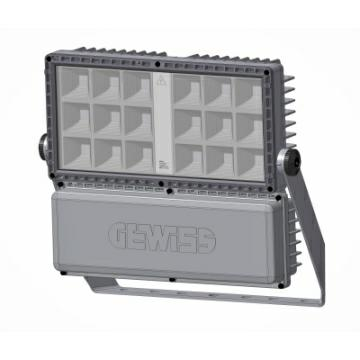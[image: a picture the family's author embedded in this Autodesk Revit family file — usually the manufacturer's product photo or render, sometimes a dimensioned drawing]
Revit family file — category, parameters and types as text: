
# Revit family: Lighting-Floodlights-GEWISS-SMART[PRO]2.0-LED-MEDIUM-POWER_1MODULE_DALI.CLI
name_source: partatom
category: Apparecchi per illuminazione
units: mm (PartAtom-declared; Revit-internal decimal feet)

## family parameters
Condiviso = No
Host = Superficie
Punto di calcolo locali = Sì
Quota connettore circolare = Usa diametro
Sorgente d'illuminazione = No
Taglio con vuoti quando caricato = No
Tipo di parte = Normale

## types (1)
- Lighting-Floodlights-GEWISS-SMART[PRO]2.0-LED-MEDIUM-POWER_1MODULE_DALI.CLI
    Applicazione = Indoor / Outdoor
    Body = Die-cast aluminium -
    Catalogue = LIGHTING
    Classification: = -
    Color Rendering Index = CRI-80
    Colour = Graphite grey
    Colour : = Polyester powder coated
    Colour temperature = 5700K
    Context = Sport, Big Areas
    Control System = DALI
    DIN 18032-3 certification = Yes
    Descrizione = SMARTPRO2.0 1M 5700K CRI80 A3 DALI CL1
    Device with reduced surface temperature = Yes
    Driver = Included
    Driver Box = Built-in
    Efficiency (lm/W) = 107
    Eletrical and lighting features = -
    External screw = Stainless steel
    Fixing = Bracket
    GW - Codice Electrocod = 2424
    Gasket = Anti-aging silicone
    General information = -
    Glow Wire Test : = -
    IDF = 6b732f17-0807-4800-995f-8617eb2233d5
    IDT = 706d4f98386b454aa472bb2581cb3bfe
    IP degree = IP66
    IPEA = ROAD = A // LARGE AREAS = A3 + // CYCLOPEDONALS = A + // GREEN AREAS = A + // HISTORICAL CENTER = A5 + // OTHER = A5 +
    Immagine tipo = SMARTPRO20_1M.jpg
    Installationa and maintenance = -
    Insulation class = I
    LED Maintenance = Not available
    Lifetime = L90B10 (Tq+25°C) - 50000h L90B10 (Tq+50°C) = 32000h L80B10 (Tq+25°C) - 110000h
    Locking Hook = Hexagonal metric screws
    Lumen output (lm) = 17600
    Luminaire = LED luminaire with small,mid and high lumen power
    Materials = -
    Maximum surface exposed to the wind : = 0,085 m2
    Modello = GWP2185ND
    Mouting and installation = High-mast lighting - Wall mounting - Ground mouting
    Operating temperature : = -30 +50 °C
    Optic = A3 - Assymetric Narrow
    Optic : = Polished anodised aluminum reflector with 99.99% pure aluminum
    Optic Maintenance = Not available
    Optic and illuminating features = -
    Overvoltage protection = DM 6 kV / CM 10 kV
    Photobiological Risk Class = -
    Produttore = GEWISS S.p.A.
    Prospetto di default = 1219 mm
    Rated frequency (Hz) = 50 / 60
    SEO = Floodlight
    Shield type = Flat tempered glass 4mm
    Shock resistance = IK08
    Standard Deviation Colour Matching = SDCM = 3
    Standard- = EN60598-1; EN60598-2-5; EN60598-2-24; IEC 62778; IEC62471; EN13201
    Standards and approvals = -
    Stocking temperature = -
    Supply voltage = 220 - 240 V
    System power = 165W
    Technical sheet = https://www.gewiss.com
    Tilt- = Rotation on bracket with integrated goniometer
    Type of light source = LED - Not replaceable
    URL = https://www.gewiss.com
    Unified Glare Rating = G*6 - ULOR = 0
    Unique digital code (Datamatrix) = Currently not present
    Version file RFA = 20.11
    Versions = 5700K cold light
    Warranty = 5 years
    Weight (kg): = 5,7
    Wiring = Watertight connector
